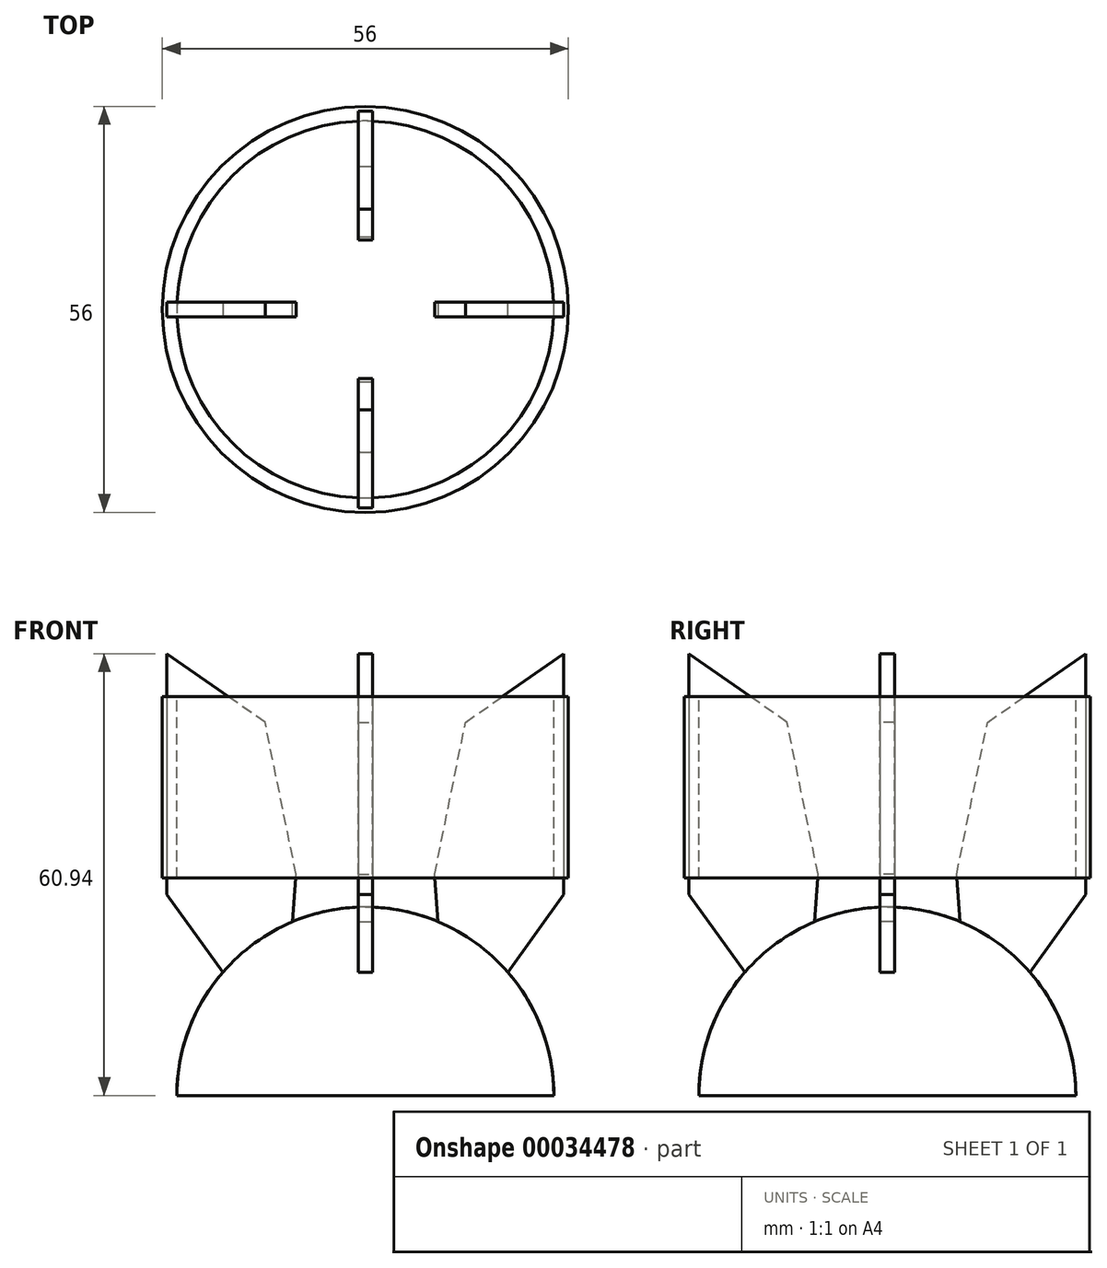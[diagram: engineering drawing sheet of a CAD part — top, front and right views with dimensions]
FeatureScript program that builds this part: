
annotation { "Feature Type Name" : "Feature", "Feature Type Description" : "" }
export const myFeature = defineFeature(function(context is Context, id is Id, definition is map)
    precondition{}
    {
        {
            var Q0;
            Q0=qCreatedBy(makeId("Top.planeOp"),FACE);
            cPlane(context, id + "F0", {"entities" : qUnion([Q0]), "cplaneType" : CPlaneType.OFFSET, "offset" : 55 * mm, "width" : 150 * mm, "height" : 150 * mm});
        }
        {
            var Q0;
            Q0=qCreatedBy(makeId("Front.planeOp"),FACE);
            var sketch = newSketch(context, id + "F1", { "sketchPlane" : qUnion([Q0])});
            skLineSegment(sketch, "E0", {"start": v(0, 0) * mm, "end": v(-26, 0) * mm});
            skLineSegment(sketch, "E1", {"start": v(0, 0) * mm, "end": v(0, 26) * mm});
            skArc(sketch, "E2", {"start": v(0, 26) * mm, "mid": v(-18.38, 18.38) * mm, "end": v(-26, 0) * mm});
            skSolve(sketch);
        }
        {
            var Q0;
            Q0=makeQuery(id+"F1.imprint","IMPRINT",FACE,{"disambiguationData":[TD([[makeQuery(id+"F1.imprint","IMPRINT",EDGE,{"derivedFrom":sQuery(id+"F1.wireOp",EDGE,"E0")}),-1.0]])]});
            var Q1;
            Q1=sQuery(id+"F1.wireOp",EDGE,"E1");
            revolve(context, id + "F2", {"entities" : qUnion([Q0]), "axis" : qUnion([Q1]), "revolveType" : RevolveType.FULL});
        }
        {
            var Q0;
            Q0=qCreatedBy(makeId("Front.planeOp"),FACE);
            var sketch = newSketch(context, id + "F3", { "sketchPlane" : qUnion([Q0])});
            skLineSegment(sketch, "E3", {"start": v(-9.56, 30.52) * mm, "end": v(-13.83, 51.48) * mm});
            skLineSegment(sketch, "E4", {"start": v(-13.83, 51.48) * mm, "end": v(-27.37, 60.94) * mm});
            skLineSegment(sketch, "E5", {"start": v(-27.37, 60.94) * mm, "end": v(-27.37, 27.73) * mm});
            skLineSegment(sketch, "E6", {"start": v(-27.37, 27.73) * mm, "end": v(-17.72, 14.3) * mm});
            skLineSegment(sketch, "E7", {"start": v(-17.72, 14.3) * mm, "end": v(-10.35, 19.6) * mm});
            skLineSegment(sketch, "E8", {"start": v(-10.35, 19.6) * mm, "end": v(-9.56, 30.52) * mm});
            skSolve(sketch);
        }
        {
            var Q0;
            Q0=makeQuery(id+"F3.imprint","IMPRINT",FACE,{"disambiguationData":[TD([[makeQuery(id+"F3.imprint","IMPRINT",EDGE,{"derivedFrom":sQuery(id+"F3.wireOp",EDGE,"E3")}),1.0]])]});
            extrude(context, id + "F4", {"entities" : qUnion([Q0]), "operationType" : NewBodyOperationType.ADD, "depth" : 1 * mm, "hasSecondDirection" : true, "secondDirectionOppositeDirection" : true, "secondDirectionDepth" : 1 * mm});
        }
        {
            var Q0;
            Q0=qCreatedBy(makeId("Front.planeOp"),FACE);
            var sketch = newSketch(context, id + "F5", { "sketchPlane" : qUnion([Q0])});
            skLineSegment(sketch, "E9", {"start": v(0, -12.15) * mm, "end": v(0, 46.84) * mm});
            skSolve(sketch);
        }
        {
            var Q0;
            Q0=makeQuery(id+"F2.opRevolve","SWEPT_BODY",BODY,{"disambiguationData":[OSD([sQuery(id+"F1.wireOp",EDGE,"E0"),sQuery(id+"F1.wireOp",EDGE,"E1"),sQuery(id+"F1.wireOp",EDGE,"E2")])]});
            var Q1;
            Q1=sQuery(id+"F5.wireOp",EDGE,"E9");
            circularPattern(context, id + "F6", {"entities" : qUnion([Q0]), "axis" : qUnion([Q1]), "angle" : 360 * degree, "instanceCount" : 4, "equalSpace" : true});
        }
        {
            var Q0;
            Q0=qCreatedBy(id+"F0.planeOp",FACE);
            var sketch = newSketch(context, id + "F7", { "sketchPlane" : qUnion([Q0])});
            skCircle(sketch, "E10", {"center": v(0, 0) * mm, "radius": 26 * mm});
            skCircle(sketch, "E11.0", {"center": v(0, 0) * mm, "radius": 28 * mm});
            skSolve(sketch);
        }
        {
            var Q0;
            Q0=makeQuery(id+"F7.imprint","IMPRINT",FACE,{"disambiguationData":[TD([[makeQuery(id+"F7.imprint","IMPRINT",EDGE,{"derivedFrom":sQuery(id+"F7.wireOp",EDGE,"E10")}),-1.0]])]});
            extrude(context, id + "F8", {"entities" : qUnion([Q0]), "oppositeDirection" : true, "depth" : 25 * mm});
        }
    });
